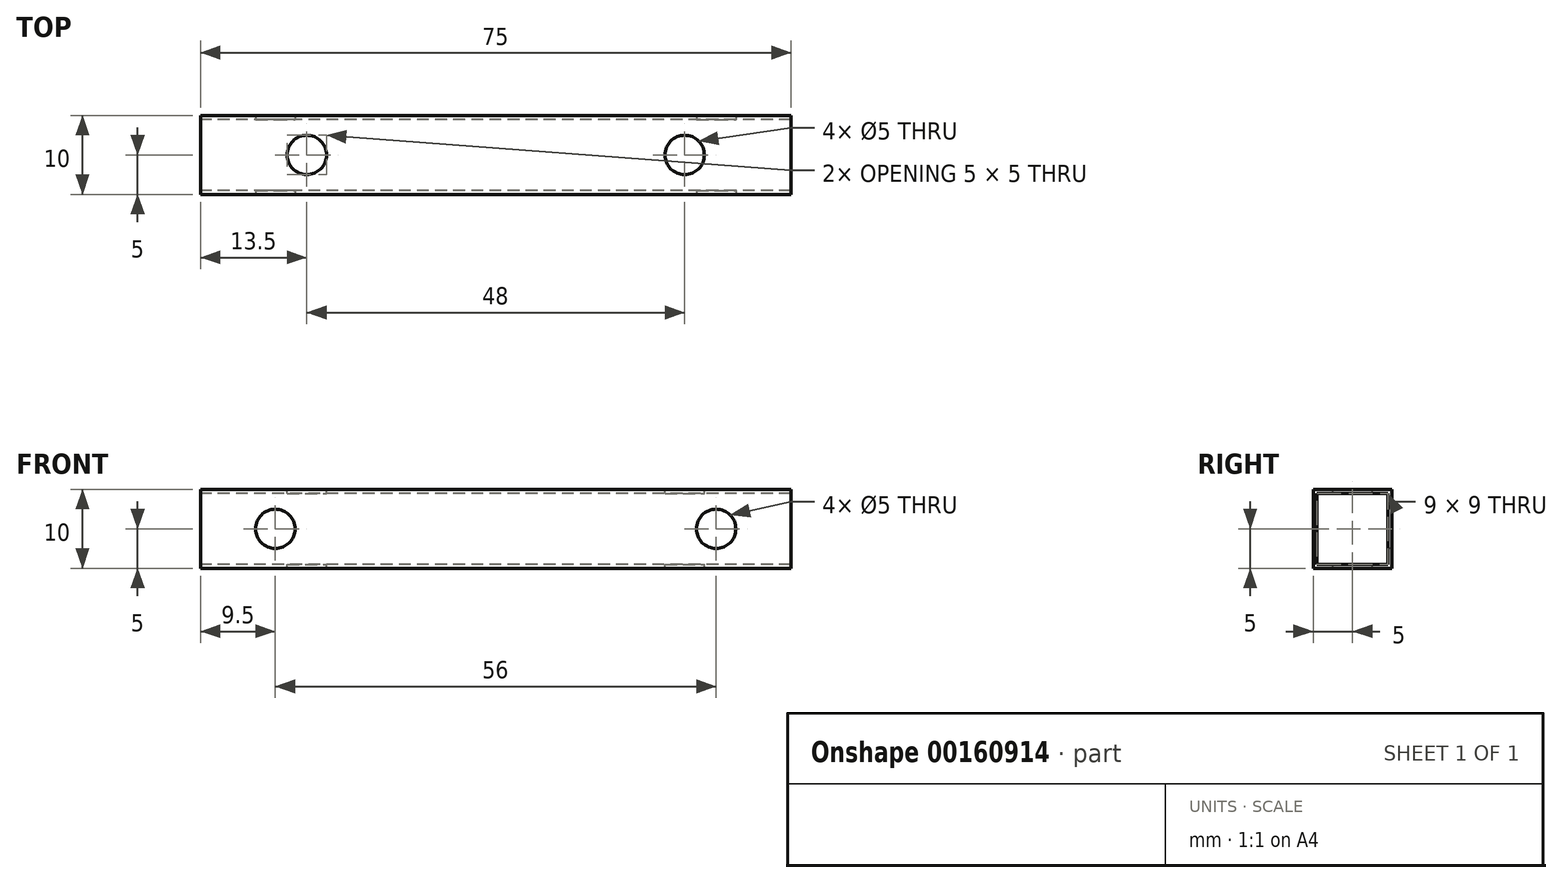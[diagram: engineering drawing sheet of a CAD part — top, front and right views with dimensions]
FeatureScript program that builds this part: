
annotation { "Feature Type Name" : "Feature", "Feature Type Description" : "" }
export const myFeature = defineFeature(function(context is Context, id is Id, definition is map)
    precondition{}
    {
        {
            var Q0;
            Q0=qCreatedBy(makeId("Right.planeOp"),FACE);
            var sketch = newSketch(context, id + "F0", { "sketchPlane" : qUnion([Q0])});
            skLineSegment(sketch, "E0.bottom", {"start": v(5, -5) * mm, "end": v(-5, -5) * mm});
            skLineSegment(sketch, "E0.top", {"start": v(5, 5) * mm, "end": v(-5, 5) * mm});
            skLineSegment(sketch, "E0.left", {"start": v(5, -5) * mm, "end": v(5, 5) * mm});
            skLineSegment(sketch, "E0.right", {"start": v(-5, -5) * mm, "end": v(-5, 5) * mm});
            skPoint(sketch, "E0.middle", {"position": v(0, 0) * mm});
            skLineSegment(sketch, "E1.bottom", {"start": v(4.5, -4.5) * mm, "end": v(-4.5, -4.5) * mm});
            skLineSegment(sketch, "E1.top", {"start": v(4.5, 4.5) * mm, "end": v(-4.5, 4.5) * mm});
            skLineSegment(sketch, "E1.left", {"start": v(4.5, -4.5) * mm, "end": v(4.5, 4.5) * mm});
            skLineSegment(sketch, "E1.right", {"start": v(-4.5, -4.5) * mm, "end": v(-4.5, 4.5) * mm});
            skSolve(sketch);
        }
        {
            var Q0;
            Q0 = qSketchRegion(id + "F0", true);
            extrude(context, id + "F1", {"entities" : qUnion([Q0]), "depth" : 37.5 * mm, "hasSecondDirection" : true, "secondDirectionOppositeDirection" : true, "secondDirectionDepth" : 37.5 * mm});
        }
        {
            var Q0;
            Q0=makeQuery(id+"F1.opExtrude","SWEPT_FACE",FACE,{"disambiguationData":[OSD([sQuery(id+"F0.wireOp",EDGE,"E0.top")])]});
            var sketch = newSketch(context, id + "F2", { "sketchPlane" : qUnion([Q0])});
            skCircle(sketch, "E2", {"center": v(-24, 0) * mm, "radius": 2.5 * mm});
            skCircle(sketch, "E3.MirrorC", {"center": v(24, 0) * mm, "radius": 2.5 * mm});
            skSolve(sketch);
        }
        {
            var Q0;
            Q0 = qSketchRegion(id + "F2", true);
            extrude(context, id + "F3", {"entities" : qUnion([Q0]), "operationType" : NewBodyOperationType.REMOVE, "oppositeDirection" : true, "depth" : 10 * mm});
        }
        {
            var Q0;
            Q0=makeQuery(id+"F1.opExtrude","SWEPT_FACE",FACE,{"disambiguationData":[OSD([sQuery(id+"F0.wireOp",EDGE,"E0.right")])]});
            var sketch = newSketch(context, id + "F4", { "sketchPlane" : qUnion([Q0])});
            skCircle(sketch, "E4", {"center": v(-28, 0) * mm, "radius": 2.5 * mm});
            skCircle(sketch, "E5.MirrorC", {"center": v(28, 0) * mm, "radius": 2.5 * mm});
            skSolve(sketch);
        }
        {
            var Q0;
            Q0 = qSketchRegion(id + "F4", true);
            extrude(context, id + "F5", {"entities" : qUnion([Q0]), "operationType" : NewBodyOperationType.REMOVE, "oppositeDirection" : true, "depth" : 10 * mm});
        }
    });
